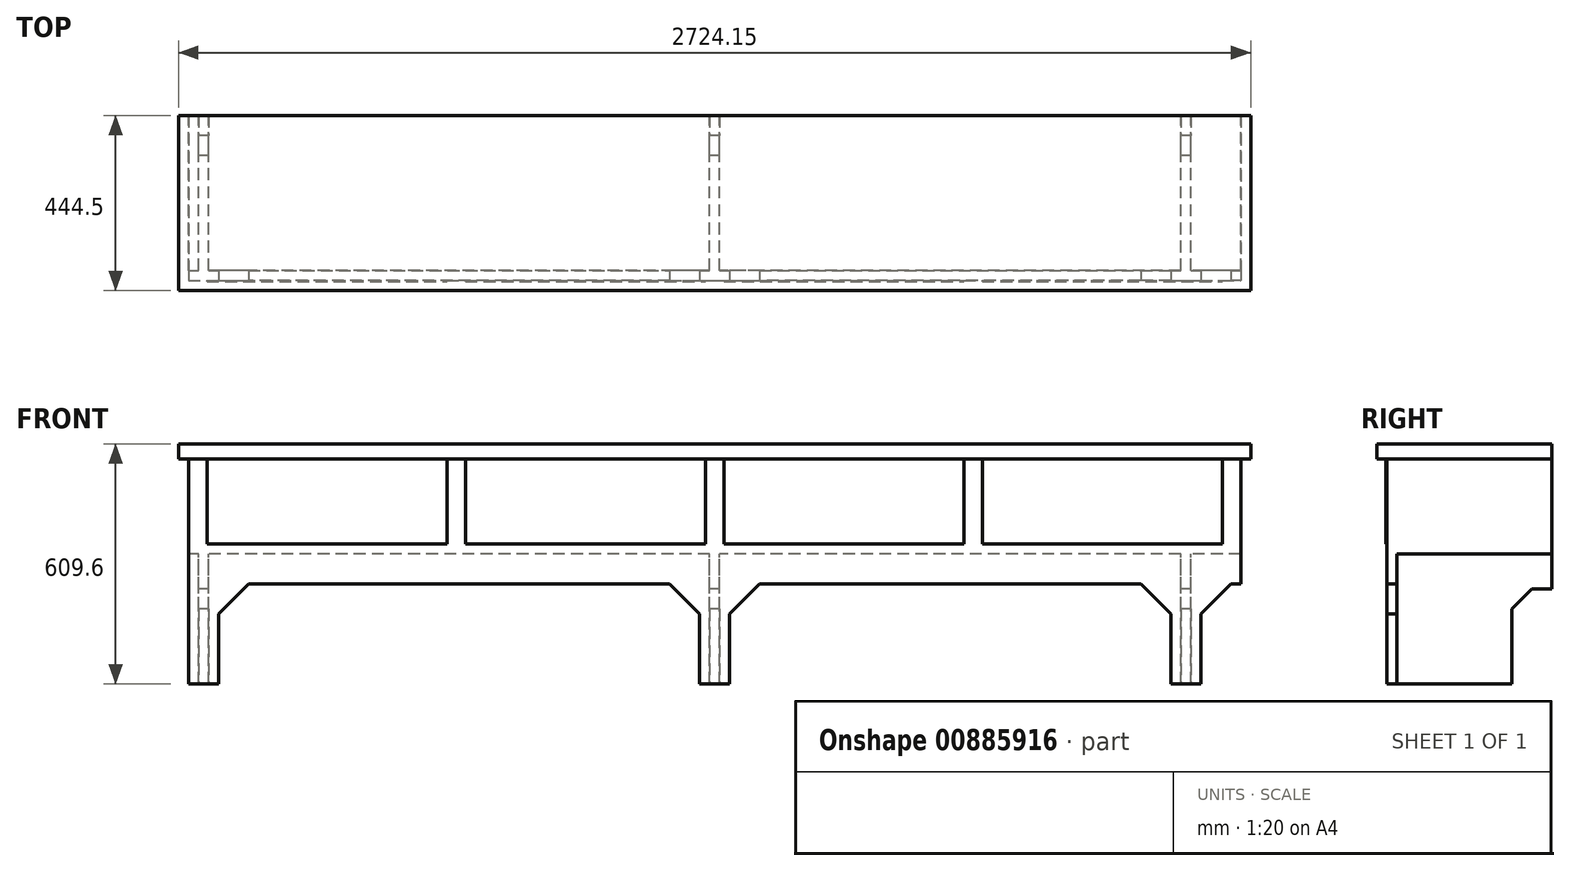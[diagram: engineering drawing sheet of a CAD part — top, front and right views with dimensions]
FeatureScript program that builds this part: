
annotation { "Feature Type Name" : "Feature", "Feature Type Description" : "" }
export const myFeature = defineFeature(function(context is Context, id is Id, definition is map)
    precondition{}
    {
        {
            var Q0;
            Q0=qCreatedBy(makeId("Top.planeOp"),FACE);
            var sketch = newSketch(context, id + "F0", { "sketchPlane" : qUnion([Q0])});
            skLineSegment(sketch, "E0.bottom", {"start": v(-1362.07, 0) * mm, "end": v(1362.07, 0) * mm});
            skLineSegment(sketch, "E0.top", {"start": v(-1362.07, -419.1) * mm, "end": v(1362.07, -419.1) * mm});
            skLineSegment(sketch, "E0.left", {"start": v(-1362.07, 0) * mm, "end": v(-1362.07, -419.1) * mm});
            skLineSegment(sketch, "E0.right", {"start": v(1362.08, 0) * mm, "end": v(1362.08, -419.1) * mm});
            skSolve(sketch);
        }
        {
            var Q0;
            Q0=makeQuery(id+"F0.imprint","IMPRINT",FACE,{"disambiguationData":[TD([[makeQuery(id+"F0.imprint","IMPRINT",EDGE,{"derivedFrom":sQuery(id+"F0.wireOp",EDGE,"E0.bottom")}),-1.0]])]});
            extrude(context, id + "F1", {"entities" : qUnion([Q0]), "oppositeDirection" : true, "depth" : 609.6 * mm, "offsetDistance" : 25.4 * mm});
        }
        {
            var Q0;
            Q0=qCreatedBy(makeId("Right.planeOp"),FACE);
            var sketch = newSketch(context, id + "F2", { "sketchPlane" : qUnion([Q0])});
            skLineSegment(sketch, "E1", {"start": v(-101.6, -609.6) * mm, "end": v(-101.6, -419.1) * mm});
            skLineSegment(sketch, "E2", {"start": v(-50.8, -368.3) * mm, "end": v(-101.6, -419.1) * mm});
            skLineSegment(sketch, "E3", {"start": v(-50.8, -368.3) * mm, "end": v(0, -368.3) * mm});
            skLineSegment(sketch, "E4", {"start": v(0, -368.3) * mm, "end": v(0, -609.6) * mm});
            skLineSegment(sketch, "E5", {"start": v(0, -609.6) * mm, "end": v(-101.6, -609.6) * mm});
            skSolve(sketch);
        }
        {
            var Q0;
            Q0 = qSketchRegion(id + "F2", true);
            extrude(context, id + "F3", {"entities" : qUnion([Q0]), "operationType" : NewBodyOperationType.REMOVE, "endBound" : BoundingType.THROUGH_ALL, "depth" : 25.4 * mm, "offsetDistance" : 25.4 * mm, "hasSecondDirection" : true, "secondDirectionBound" : SecondDirectionBoundingType.THROUGH_ALL, "secondDirectionOppositeDirection" : true, "secondDirectionDepth" : 25.4 * mm});
        }
        {
            var Q0;
            Q0=makeQuery(id+"F1.opExtrude","SWEPT_FACE",FACE,{"disambiguationData":[OSD([sQuery(id+"F0.wireOp",EDGE,"E0.top")])]});
            var sketch = newSketch(context, id + "F4", { "sketchPlane" : qUnion([Q0])});
            skLineSegment(sketch, "E6.bottom", {"start": v(1362.08, -38.1) * mm, "end": v(1336.68, -38.1) * mm});
            skLineSegment(sketch, "E6.top", {"start": v(1362.08, -609.6) * mm, "end": v(1336.68, -609.6) * mm});
            skLineSegment(sketch, "E6.left", {"start": v(1362.08, -38.1) * mm, "end": v(1362.08, -609.6) * mm});
            skLineSegment(sketch, "E6.right", {"start": v(1336.68, -38.1) * mm, "end": v(1336.68, -609.6) * mm});
            skLineSegment(sketch, "E7.bottom", {"start": v(-1362.07, -38.1) * mm, "end": v(-1336.67, -38.1) * mm});
            skLineSegment(sketch, "E7.top", {"start": v(-1362.07, -609.6) * mm, "end": v(-1336.67, -609.6) * mm});
            skLineSegment(sketch, "E7.left", {"start": v(-1362.07, -38.1) * mm, "end": v(-1362.07, -609.6) * mm});
            skLineSegment(sketch, "E7.right", {"start": v(-1336.67, -38.1) * mm, "end": v(-1336.67, -609.6) * mm});
            skSolve(sketch);
        }
        {
            var Q0;
            Q0 = qSketchRegion(id + "F4", true);
            extrude(context, id + "F5", {"entities" : qUnion([Q0]), "operationType" : NewBodyOperationType.REMOVE, "endBound" : BoundingType.THROUGH_ALL, "oppositeDirection" : true, "depth" : 25.4 * mm, "offsetDistance" : 25.4 * mm});
        }
        {
            var Q0;
            Q0=makeQuery(id+"F1.opExtrude","SWEPT_FACE",FACE,{"disambiguationData":[OSD([sQuery(id+"F0.wireOp",EDGE,"E0.top")])]});
            var sketch = newSketch(context, id + "F6", { "sketchPlane" : qUnion([Q0])});
            skLineSegment(sketch, "E8.bottom", {"start": v(-1260.47, -609.6) * mm, "end": v(-38.1, -609.6) * mm});
            skLineSegment(sketch, "E8.left", {"start": v(-1260.47, -609.6) * mm, "end": v(-1260.47, -431.8) * mm});
            skLineSegment(sketch, "E8.right", {"start": v(-38.1, -609.6) * mm, "end": v(-38.1, -431.8) * mm});
            skLineSegment(sketch, "E9.bottom", {"start": v(38.1, -609.6) * mm, "end": v(1158.88, -609.6) * mm});
            skLineSegment(sketch, "E9.left", {"start": v(38.1, -609.6) * mm, "end": v(38.1, -431.8) * mm});
            skLineSegment(sketch, "E9.right", {"start": v(1158.88, -609.6) * mm, "end": v(1158.88, -431.8) * mm});
            skLineSegment(sketch, "E10", {"start": v(-38.1, 0) * mm, "end": v(38.1, 0) * mm, "construction": true});
            skLineSegment(sketch, "E11", {"start": v(-1260.47, -609.6) * mm, "end": v(-1336.67, -609.6) * mm, "construction": true});
            skLineSegment(sketch, "E12", {"start": v(1158.88, -609.6) * mm, "end": v(1235.08, -609.6) * mm, "construction": true});
            skLineSegment(sketch, "E13", {"start": v(1082.68, -355.6) * mm, "end": v(114.3, -355.6) * mm});
            skLineSegment(sketch, "E14", {"start": v(-114.3, -355.6) * mm, "end": v(-1184.28, -355.6) * mm});
            skLineSegment(sketch, "E15", {"start": v(-1260.48, -431.8) * mm, "end": v(-1184.28, -355.6) * mm});
            skLineSegment(sketch, "E16", {"start": v(-114.3, -355.6) * mm, "end": v(-38.1, -431.8) * mm});
            skLineSegment(sketch, "E17", {"start": v(38.1, -431.8) * mm, "end": v(114.3, -355.6) * mm});
            skLineSegment(sketch, "E18", {"start": v(1158.88, -431.8) * mm, "end": v(1082.68, -355.6) * mm});
            skLineSegment(sketch, "E19", {"start": v(-649.29, -355.6) * mm, "end": v(-649.29, -609.6) * mm, "construction": true});
            skLineSegment(sketch, "E20", {"start": v(598.49, -355.6) * mm, "end": v(598.49, -609.6) * mm, "construction": true});
            skLineSegment(sketch, "E21", {"start": v(1235.08, -609.6) * mm, "end": v(1235.08, -431.8) * mm});
            skLineSegment(sketch, "E22", {"start": v(1235.08, -431.8) * mm, "end": v(1311.28, -355.6) * mm});
            skLineSegment(sketch, "E23", {"start": v(1336.68, -355.6) * mm, "end": v(1336.68, -609.6) * mm});
            skLineSegment(sketch, "E24", {"start": v(1336.68, -609.6) * mm, "end": v(1235.08, -609.6) * mm});
            skLineSegment(sketch, "E25", {"start": v(1336.68, -355.6) * mm, "end": v(1311.28, -355.6) * mm});
            skSolve(sketch);
        }
        {
            var Q0;
            Q0 = qSketchRegion(id + "F6", true);
            extrude(context, id + "F7", {"entities" : qUnion([Q0]), "operationType" : NewBodyOperationType.REMOVE, "endBound" : BoundingType.THROUGH_ALL, "oppositeDirection" : true, "depth" : 25.4 * mm, "offsetDistance" : 25.4 * mm});
        }
        {
            var Q0;
            Q0=makeQuery(id+"F1.opExtrude","SWEPT_FACE",FACE,{"disambiguationData":[OSD([sQuery(id+"F0.wireOp",EDGE,"E0.top")])]});
            var sketch = newSketch(context, id + "F8", { "sketchPlane" : qUnion([Q0])});
            skLineSegment(sketch, "E26.bottom", {"start": v(-1289.68, -38.1) * mm, "end": v(-680.09, -38.1) * mm});
            skLineSegment(sketch, "E26.top", {"start": v(-1289.68, -254) * mm, "end": v(-680.09, -254) * mm});
            skLineSegment(sketch, "E26.left", {"start": v(-1289.68, -38.1) * mm, "end": v(-1289.68, -254) * mm});
            skLineSegment(sketch, "E26.right", {"start": v(-680.09, -38.1) * mm, "end": v(-680.09, -254) * mm});
            skLineSegment(sketch, "E27.bottom", {"start": v(-633.1, -38.1) * mm, "end": v(-23.5, -38.1) * mm});
            skLineSegment(sketch, "E27.top", {"start": v(-633.1, -254) * mm, "end": v(-23.5, -254) * mm});
            skLineSegment(sketch, "E27.left", {"start": v(-633.1, -38.1) * mm, "end": v(-633.1, -254) * mm});
            skLineSegment(sketch, "E27.right", {"start": v(-23.5, -38.1) * mm, "end": v(-23.5, -254) * mm});
            skLineSegment(sketch, "E28.bottom", {"start": v(23.5, -38.1) * mm, "end": v(633.1, -38.1) * mm});
            skLineSegment(sketch, "E28.top", {"start": v(23.5, -254) * mm, "end": v(633.1, -254) * mm});
            skLineSegment(sketch, "E28.left", {"start": v(23.5, -38.1) * mm, "end": v(23.5, -254) * mm});
            skLineSegment(sketch, "E28.right", {"start": v(633.1, -38.1) * mm, "end": v(633.1, -254) * mm});
            skLineSegment(sketch, "E29.bottom", {"start": v(680.09, -38.1) * mm, "end": v(1289.68, -38.1) * mm});
            skLineSegment(sketch, "E29.top", {"start": v(680.09, -254) * mm, "end": v(1289.68, -254) * mm});
            skLineSegment(sketch, "E29.left", {"start": v(680.09, -38.1) * mm, "end": v(680.09, -254) * mm});
            skLineSegment(sketch, "E29.right", {"start": v(1289.68, -38.1) * mm, "end": v(1289.68, -254) * mm});
            skLineSegment(sketch, "E30", {"start": v(-1336.67, -254) * mm, "end": v(-1289.68, -254) * mm, "construction": true});
            skLineSegment(sketch, "E31", {"start": v(-680.09, -254) * mm, "end": v(-633.1, -254) * mm, "construction": true});
            skLineSegment(sketch, "E32", {"start": v(-23.5, -254) * mm, "end": v(23.5, -254) * mm, "construction": true});
            skLineSegment(sketch, "E33", {"start": v(633.1, -254) * mm, "end": v(680.09, -254) * mm, "construction": true});
            skLineSegment(sketch, "E34", {"start": v(0, 0) * mm, "end": v(0, -254) * mm, "construction": true});
            skSolve(sketch);
        }
        {
            var Q0;
            Q0 = qSketchRegion(id + "F8", true);
            extrude(context, id + "F9", {"entities" : qUnion([Q0]), "operationType" : NewBodyOperationType.ADD, "depth" : 2.54 * mm, "offsetDistance" : 25.4 * mm});
        }
        {
            var Q0;
            Q0=makeQuery(id+"F1.opExtrude","SWEPT_FACE",FACE,{"disambiguationData":[OSD([sQuery(id+"F0.wireOp",EDGE,"E0.bottom")])]});
            var sketch = newSketch(context, id + "F10", { "sketchPlane" : qUnion([Q0])});
            skLineSegment(sketch, "E35.bottom", {"start": v(-1209.68, -609.6) * mm, "end": v(-1184.28, -609.6) * mm});
            skLineSegment(sketch, "E35.left", {"start": v(-1209.68, -609.6) * mm, "end": v(-1209.68, -279.4) * mm});
            skLineSegment(sketch, "E35.right", {"start": v(-1184.28, -609.6) * mm, "end": v(-1184.28, -279.4) * mm});
            skLineSegment(sketch, "E36.bottom", {"start": v(-12.7, -609.6) * mm, "end": v(12.7, -609.6) * mm});
            skLineSegment(sketch, "E36.left", {"start": v(-12.7, -609.6) * mm, "end": v(-12.7, -279.4) * mm});
            skLineSegment(sketch, "E36.right", {"start": v(12.7, -609.6) * mm, "end": v(12.7, -279.4) * mm});
            skLineSegment(sketch, "E37.bottom", {"start": v(1285.88, -609.6) * mm, "end": v(1311.28, -609.6) * mm});
            skLineSegment(sketch, "E37.left", {"start": v(1285.88, -609.6) * mm, "end": v(1285.88, -279.4) * mm});
            skLineSegment(sketch, "E37.right", {"start": v(1311.28, -609.6) * mm, "end": v(1311.28, -279.4) * mm});
            skLineSegment(sketch, "E38", {"start": v(-1336.68, -279.4) * mm, "end": v(-1209.68, -279.4) * mm});
            skLineSegment(sketch, "E39.trimOffspring", {"start": v(-1184.28, -279.4) * mm, "end": v(-12.7, -279.4) * mm});
            skLineSegment(sketch, "E40.trimOffspring", {"start": v(12.7, -279.4) * mm, "end": v(1285.88, -279.4) * mm});
            skLineSegment(sketch, "E41.trimOffspring", {"start": v(1311.28, -279.4) * mm, "end": v(1336.67, -279.4) * mm});
            skLineSegment(sketch, "E42", {"start": v(-1336.68, -279.4) * mm, "end": v(-1336.68, -635) * mm});
            skLineSegment(sketch, "E43", {"start": v(-1336.68, -635) * mm, "end": v(1336.67, -635) * mm});
            skLineSegment(sketch, "E44", {"start": v(1336.67, -635) * mm, "end": v(1336.67, -279.4) * mm});
            skSolve(sketch);
        }
        {
            var Q0;
            Q0 = qSketchRegion(id + "F10", true);
            var Q1;
            Q1=makeQuery(id+"F1.opExtrude","SWEPT_FACE",FACE,{"disambiguationData":[OSD([sQuery(id+"F0.wireOp",EDGE,"E0.top")])]});
            extrude(context, id + "F11", {"entities" : qUnion([Q0]), "operationType" : NewBodyOperationType.REMOVE, "endBound" : BoundingType.UP_TO_SURFACE, "oppositeDirection" : true, "depth" : 25.4 * mm, "endBoundEntityFace" : qUnion([Q1]), "hasOffset" : true, "offsetDistance" : 25.4 * mm});
        }
        {
            var Q0;
            Q0=makeQuery(id+"F1.opExtrude","SWEPT_FACE",FACE,{"disambiguationData":[OSD([sQuery(id+"F0.wireOp",EDGE,"E0.top")])]});
            var sketch = newSketch(context, id + "F12", { "sketchPlane" : qUnion([Q0])});
            skLineSegment(sketch, "E45.bottom", {"start": v(-1362.07, 0) * mm, "end": v(1362.08, 0) * mm});
            skLineSegment(sketch, "E45.top", {"start": v(-1362.07, -38.1) * mm, "end": v(1362.08, -38.1) * mm});
            skLineSegment(sketch, "E45.left", {"start": v(-1362.07, 0) * mm, "end": v(-1362.07, -38.1) * mm});
            skLineSegment(sketch, "E45.right", {"start": v(1362.08, 0) * mm, "end": v(1362.08, -38.1) * mm});
            skSolve(sketch);
        }
        {
            var Q0;
            Q0 = qSketchRegion(id + "F12", true);
            extrude(context, id + "F13", {"entities" : qUnion([Q0]), "operationType" : NewBodyOperationType.ADD, "depth" : 25.4 * mm, "offsetDistance" : 25.4 * mm});
        }
        {
            var Q0;
            Q0=qCreatedBy(makeId("Front.planeOp"),FACE);
            var sketch = newSketch(context, id + "F14", { "sketchPlane" : qUnion([Q0])});
            skLineSegment(sketch, "E46.bottom", {"start": v(-1336.68, 654.05) * mm, "end": v(-828.68, 654.05) * mm});
            skLineSegment(sketch, "E46.left", {"start": v(-1336.67, 654.05) * mm, "end": v(-1336.67, 0) * mm});
            skLineSegment(sketch, "E46.right", {"start": v(-828.68, 654.05) * mm, "end": v(-828.68, 0) * mm});
            skLineSegment(sketch, "E47", {"start": v(-1317.62, 635) * mm, "end": v(-1317.62, 0) * mm});
            skLineSegment(sketch, "E48", {"start": v(-1317.62, 0) * mm, "end": v(-1336.67, 0) * mm});
            skLineSegment(sketch, "E49", {"start": v(-1317.62, 635) * mm, "end": v(-847.73, 635) * mm});
            skLineSegment(sketch, "E50", {"start": v(-847.73, 635) * mm, "end": v(-847.73, 0) * mm});
            skLineSegment(sketch, "E51", {"start": v(-847.73, 0) * mm, "end": v(-828.68, 0) * mm});
            skLineSegment(sketch, "E52", {"start": v(-1082.67, 635) * mm, "end": v(-1082.67, 654.05) * mm, "construction": true});
            skSolve(sketch);
        }
        {
            var Q0;
            Q0 = qSketchRegion(id + "F14", true);
            extrude(context, id + "F15", {"entities" : qUnion([Q0]), "depth" : 406.4 * mm, "offsetDistance" : 25.4 * mm});
        }
        {
            var Q0;
            Q0=makeQuery(id+"F15.opExtrude","SWEPT_BODY",BODY,{"disambiguationData":[OSD([sQuery(id+"F14.wireOp",EDGE,"E46.bottom"),sQuery(id+"F14.wireOp",EDGE,"E46.left"),sQuery(id+"F14.wireOp",EDGE,"E46.right"),sQuery(id+"F14.wireOp",EDGE,"E47"),sQuery(id+"F14.wireOp",EDGE,"E48"),sQuery(id+"F14.wireOp",EDGE,"E49"),sQuery(id+"F14.wireOp",EDGE,"E50"),sQuery(id+"F14.wireOp",EDGE,"E51")])]});
            deleteBodies(context, id + "F16", {"entities" : qUnion([Q0])});
        }
    });
